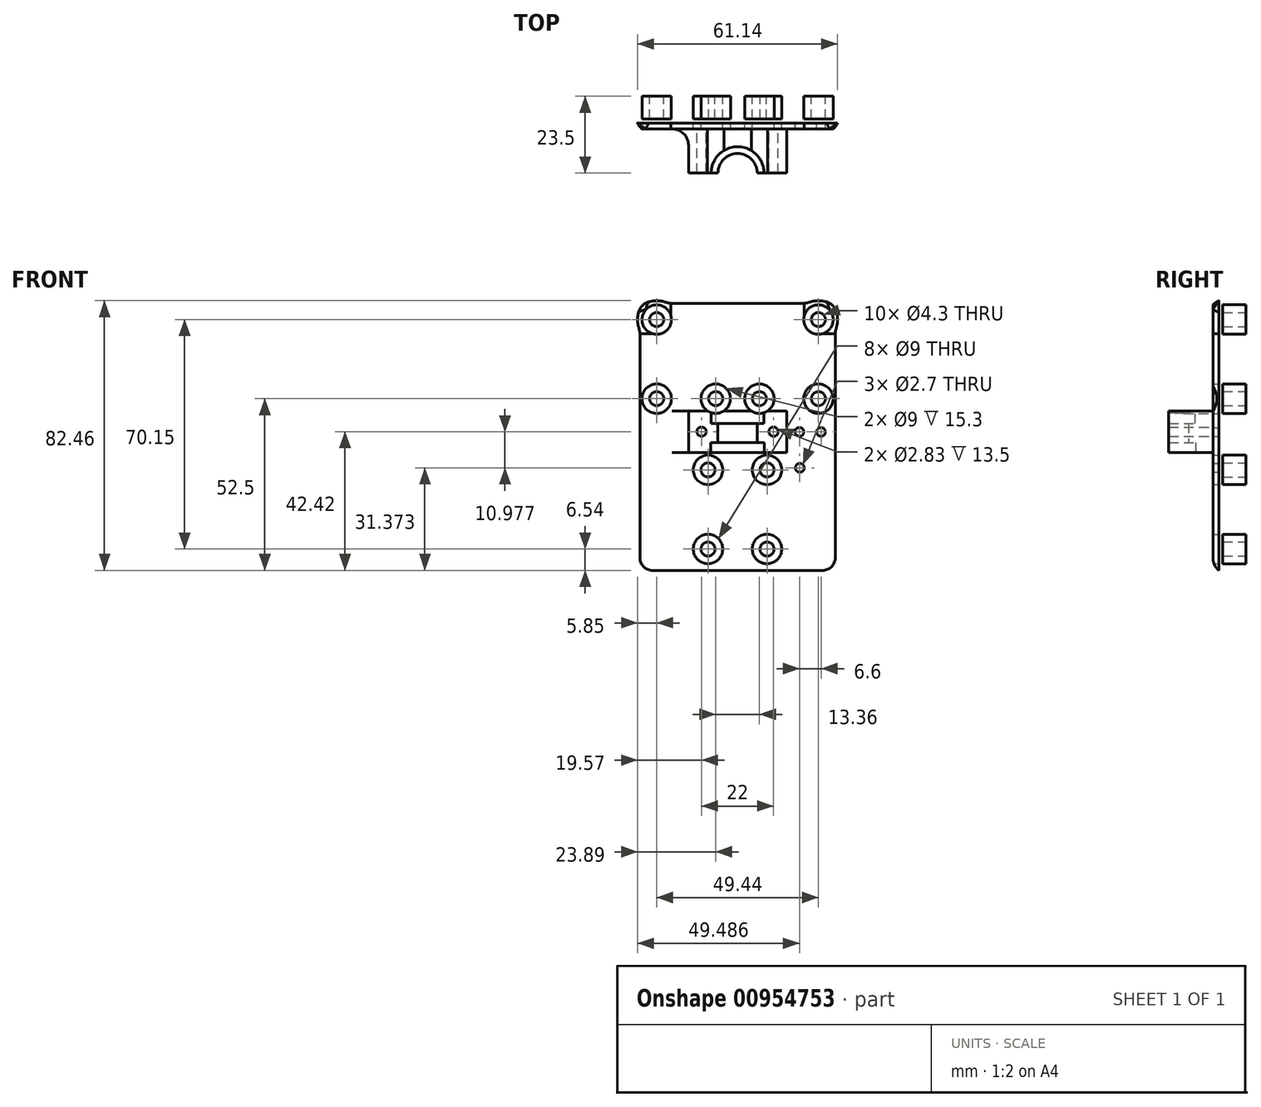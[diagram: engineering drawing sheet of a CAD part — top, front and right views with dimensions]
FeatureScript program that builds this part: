
annotation { "Feature Type Name" : "Feature", "Feature Type Description" : "" }
export const myFeature = defineFeature(function(context is Context, id is Id, definition is map)
    precondition{}
    {
        {
            var Q0;
            Q0=qCreatedBy(makeId("Front.planeOp"),FACE);
            var sketch = newSketch(context, id + "F0", { "sketchPlane" : qUnion([Q0])});
            skLineSegment(sketch, "E0.bottom", {"start": v(26, 42) * mm, "end": v(-26, 42) * mm});
            skLineSegment(sketch, "E0.top", {"start": v(26, -42) * mm, "end": v(-26, -42) * mm});
            skLineSegment(sketch, "E0.left", {"start": v(31, 37) * mm, "end": v(31, -37) * mm});
            skLineSegment(sketch, "E0.right", {"start": v(-31, 37) * mm, "end": v(-31, -37) * mm});
            skPoint(sketch, "E0.middle", {"position": v(1.18, -1.15) * mm});
            skPoint(sketch, "E1.visualSharp", {"position": v(-31, 42) * mm});
            skArc(sketch, "E1.filletArc", {"start": v(-26, 42) * mm, "mid": v(-29.54, 40.54) * mm, "end": v(-31, 37) * mm});
            skPoint(sketch, "E2.visualSharp", {"position": v(31, 42) * mm});
            skArc(sketch, "E2.filletArc", {"start": v(31, 37) * mm, "mid": v(29.54, 40.54) * mm, "end": v(26, 42) * mm});
            skPoint(sketch, "E3.visualSharp", {"position": v(31, -42) * mm});
            skArc(sketch, "E3.filletArc", {"start": v(26, -42) * mm, "mid": v(29.54, -40.54) * mm, "end": v(31, -37) * mm});
            skPoint(sketch, "E4.visualSharp", {"position": v(-31, -42) * mm});
            skArc(sketch, "E4.filletArc", {"start": v(-31, -37) * mm, "mid": v(-29.54, -40.54) * mm, "end": v(-26, -42) * mm});
            skCircle(sketch, "E5", {"center": v(-24.72, 35.85) * mm, "radius": 2.15 * mm});
            skCircle(sketch, "E6.0", {"center": v(-24.72, 35.85) * mm, "radius": 4.5 * mm});
            skCircle(sketch, "E7.1.0.0", {"center": v(-24.72, 11.66) * mm, "radius": 4.5 * mm});
            skCircle(sketch, "E7.1.0.1", {"center": v(-24.72, 11.66) * mm, "radius": 2.15 * mm});
            skCircle(sketch, "E7.1.0.2", {"center": v(-6.68, 11.66) * mm, "radius": 2.15 * mm});
            skCircle(sketch, "E7.1.0.3", {"center": v(-6.68, 11.66) * mm, "radius": 4.5 * mm});
            skCircle(sketch, "E8.1.0.2", {"center": v(6.68, 11.66) * mm, "radius": 4.5 * mm});
            skCircle(sketch, "E8.1.0.4", {"center": v(24.72, 11.66) * mm, "radius": 2.15 * mm});
            skCircle(sketch, "E8.1.0.5", {"center": v(6.68, 11.66) * mm, "radius": 2.15 * mm});
            skCircle(sketch, "E8.1.0.6", {"center": v(24.72, 35.85) * mm, "radius": 2.15 * mm});
            skCircle(sketch, "E8.1.0.7", {"center": v(24.72, 35.85) * mm, "radius": 4.5 * mm});
            skCircle(sketch, "E8.1.0.9", {"center": v(24.72, 11.66) * mm, "radius": 4.5 * mm});
            skCircle(sketch, "E9.1.0.0", {"center": v(-9.04, -10.1) * mm, "radius": 4.5 * mm});
            skCircle(sketch, "E9.1.0.1", {"center": v(-9.04, -10.1) * mm, "radius": 2.15 * mm});
            skCircle(sketch, "E9.1.0.2", {"center": v(9, -10.1) * mm, "radius": 2.15 * mm});
            skCircle(sketch, "E9.1.0.4", {"center": v(9, -10.1) * mm, "radius": 4.5 * mm});
            skCircle(sketch, "E9.1.0.6", {"center": v(-9.04, -34.3) * mm, "radius": 4.5 * mm});
            skCircle(sketch, "E9.1.0.7", {"center": v(9, -34.3) * mm, "radius": 4.5 * mm});
            skCircle(sketch, "E9.1.0.8", {"center": v(9, -34.3) * mm, "radius": 2.15 * mm});
            skCircle(sketch, "E9.1.0.9", {"center": v(-9.04, -34.3) * mm, "radius": 2.15 * mm});
            skCircle(sketch, "E10", {"center": v(-18.96, 1.51) * mm, "radius": 1.35 * mm});
            skCircle(sketch, "E11", {"center": v(-25.56, 1.51) * mm, "radius": 1.35 * mm});
            skCircle(sketch, "E12", {"center": v(-19.06, -9.47) * mm, "radius": 1.35 * mm});
            skCircle(sketch, "E13.MirrorC", {"center": v(18.92, 1.51) * mm, "radius": 1.35 * mm});
            skCircle(sketch, "E14.MirrorC", {"center": v(25.52, 1.51) * mm, "radius": 1.35 * mm});
            skCircle(sketch, "E15.MirrorC", {"center": v(19.01, -9.47) * mm, "radius": 1.35 * mm});
            skSolve(sketch);
        }
        {
            var Q0;
            Q0=makeQuery(id+"F0.imprint","IMPRINT",FACE,{"disambiguationData":[TD([[makeQuery(id+"F0.imprint","IMPRINT",EDGE,{"derivedFrom":sQuery(id+"F0.wireOp",EDGE,"E0.bottom")}),1.0]])]});
            var Q1;
            Q1=makeQuery(id+"F0.imprint","IMPRINT",FACE,{"disambiguationData":[TD([[makeQuery(id+"F0.imprint","IMPRINT",EDGE,{"derivedFrom":sQuery(id+"F0.wireOp",EDGE,"E11")}),1.0]])]});
            var Q2;
            Q2=makeQuery(id+"F0.imprint","IMPRINT",FACE,{"disambiguationData":[TD([[makeQuery(id+"F0.imprint","IMPRINT",EDGE,{"derivedFrom":sQuery(id+"F0.wireOp",EDGE,"E10")}),1.0]])]});
            var Q3;
            Q3=makeQuery(id+"F0.imprint","IMPRINT",FACE,{"disambiguationData":[TD([[makeQuery(id+"F0.imprint","IMPRINT",EDGE,{"derivedFrom":sQuery(id+"F0.wireOp",EDGE,"E12")}),1.0]])]});
            var Q4;
            Q4=makeQuery(id+"F0.imprint","IMPRINT",FACE,{"disambiguationData":[TD([[makeQuery(id+"F0.imprint","IMPRINT",EDGE,{"derivedFrom":sQuery(id+"F0.wireOp",EDGE,"E13.MirrorC")}),-1.0]])]});
            var Q5;
            Q5=makeQuery(id+"F0.imprint","IMPRINT",FACE,{"disambiguationData":[TD([[makeQuery(id+"F0.imprint","IMPRINT",EDGE,{"derivedFrom":sQuery(id+"F0.wireOp",EDGE,"E14.MirrorC")}),-1.0]])]});
            var Q6;
            Q6=makeQuery(id+"F0.imprint","IMPRINT",FACE,{"disambiguationData":[TD([[makeQuery(id+"F0.imprint","IMPRINT",EDGE,{"derivedFrom":sQuery(id+"F0.wireOp",EDGE,"E15.MirrorC")}),-1.0]])]});
            extrude(context, id + "F1", {"entities" : qUnion([Q0, Q1, Q2, Q3, Q4, Q5, Q6]), "depth" : 10 * mm});
        }
        {
            var Q0;
            Q0=makeQuery(id+"F0.imprint","IMPRINT",FACE,{"disambiguationData":[TD([[makeQuery(id+"F0.imprint","IMPRINT",EDGE,{"derivedFrom":sQuery(id+"F0.wireOp",EDGE,"E5")}),-1.0]])]});
            var Q1;
            Q1=makeQuery(id+"F0.imprint","IMPRINT",FACE,{"disambiguationData":[TD([[makeQuery(id+"F0.imprint","IMPRINT",EDGE,{"derivedFrom":sQuery(id+"F0.wireOp",EDGE,"92a26904-eb14-4965-84a8-ee2cf7e59395.1.0.0")}),-1.0]])]});
            var Q2;
            Q2=makeQuery(id+"F0.imprint","IMPRINT",FACE,{"disambiguationData":[TD([[makeQuery(id+"F0.imprint","IMPRINT",EDGE,{"derivedFrom":sQuery(id+"F0.wireOp",EDGE,"E8.1.0.0")}),1.0]])]});
            var Q3;
            Q3=makeQuery(id+"F0.imprint","IMPRINT",FACE,{"disambiguationData":[TD([[makeQuery(id+"F0.imprint","IMPRINT",EDGE,{"derivedFrom":sQuery(id+"F0.wireOp",EDGE,"E7.1.0.0")}),1.0]])]});
            var Q4;
            Q4=makeQuery(id+"F0.imprint","IMPRINT",FACE,{"disambiguationData":[TD([[makeQuery(id+"F0.imprint","IMPRINT",EDGE,{"derivedFrom":sQuery(id+"F0.wireOp",EDGE,"E7.1.0.2")}),-1.0]])]});
            var Q5;
            Q5=makeQuery(id+"F0.imprint","IMPRINT",FACE,{"disambiguationData":[TD([[makeQuery(id+"F0.imprint","IMPRINT",EDGE,{"derivedFrom":sQuery(id+"F0.wireOp",EDGE,"E8.1.0.2")}),1.0]])]});
            var Q6;
            Q6=makeQuery(id+"F0.imprint","IMPRINT",FACE,{"disambiguationData":[TD([[makeQuery(id+"F0.imprint","IMPRINT",EDGE,{"derivedFrom":sQuery(id+"F0.wireOp",EDGE,"E8.1.0.6")}),-1.0]])]});
            var Q7;
            Q7=makeQuery(id+"F0.imprint","IMPRINT",FACE,{"disambiguationData":[TD([[makeQuery(id+"F0.imprint","IMPRINT",EDGE,{"derivedFrom":sQuery(id+"F0.wireOp",EDGE,"E8.1.0.4")}),-1.0]])]});
            var Q8;
            Q8=makeQuery(id+"F0.imprint","IMPRINT",FACE,{"disambiguationData":[TD([[makeQuery(id+"F0.imprint","IMPRINT",EDGE,{"derivedFrom":sQuery(id+"F0.wireOp",EDGE,"E9.1.0.6")}),1.0]])]});
            var Q9;
            Q9=makeQuery(id+"F0.imprint","IMPRINT",FACE,{"disambiguationData":[TD([[makeQuery(id+"F0.imprint","IMPRINT",EDGE,{"derivedFrom":sQuery(id+"F0.wireOp",EDGE,"E9.1.0.7")}),1.0]])]});
            var Q10;
            Q10=makeQuery(id+"F0.imprint","IMPRINT",FACE,{"disambiguationData":[TD([[makeQuery(id+"F0.imprint","IMPRINT",EDGE,{"derivedFrom":sQuery(id+"F0.wireOp",EDGE,"E9.1.0.0")}),1.0]])]});
            var Q11;
            Q11=makeQuery(id+"F0.imprint","IMPRINT",FACE,{"disambiguationData":[TD([[makeQuery(id+"F0.imprint","IMPRINT",EDGE,{"derivedFrom":sQuery(id+"F0.wireOp",EDGE,"E9.1.0.2")}),-1.0]])]});
            extrude(context, id + "F2", {"entities" : qUnion([Q0, Q1, Q2, Q3, Q4, Q5, Q6, Q7, Q8, Q9, Q10, Q11]), "operationType" : NewBodyOperationType.ADD, "depth" : 7 * mm});
        }
        {
            var Q0;
            Q0=makeQuery(id+"F1.opExtrude","CAP_FACE",FACE,{"disambiguationData":[OSD([sQuery(id+"F0.wireOp",EDGE,"E0.bottom"),sQuery(id+"F0.wireOp",EDGE,"E0.top"),sQuery(id+"F0.wireOp",EDGE,"E0.left"),sQuery(id+"F0.wireOp",EDGE,"E0.right"),sQuery(id+"F0.wireOp",EDGE,"E1.filletArc"),sQuery(id+"F0.wireOp",EDGE,"E2.filletArc"),sQuery(id+"F0.wireOp",EDGE,"E3.filletArc"),sQuery(id+"F0.wireOp",EDGE,"E4.filletArc"),sQuery(id+"F0.wireOp",EDGE,"E6.0"),sQuery(id+"F0.wireOp",EDGE,"92a26904-eb14-4965-84a8-ee2cf7e59395.1.0.1"),sQuery(id+"F0.wireOp",EDGE,"E7.1.0.0"),sQuery(id+"F0.wireOp",EDGE,"E7.1.0.3"),sQuery(id+"F0.wireOp",EDGE,"E8.1.0.0"),sQuery(id+"F0.wireOp",EDGE,"E8.1.0.2"),sQuery(id+"F0.wireOp",EDGE,"E8.1.0.7"),sQuery(id+"F0.wireOp",EDGE,"E8.1.0.9"),sQuery(id+"F0.wireOp",EDGE,"E9.1.0.0"),sQuery(id+"F0.wireOp",EDGE,"E9.1.0.4"),sQuery(id+"F0.wireOp",EDGE,"E9.1.0.6"),sQuery(id+"F0.wireOp",EDGE,"E9.1.0.7")])],"isStart":false});
            var sketch = newSketch(context, id + "F3", { "sketchPlane" : qUnion([Q0])});
            skLineSegment(sketch, "E16", {"start": v(-26, -42) * mm, "end": v(0, -42) * mm});
            skLineSegment(sketch, "E17", {"start": v(0, -42) * mm, "end": v(26, -42) * mm});
            skLineSegment(sketch, "E18.bottom", {"start": v(15, 7.92) * mm, "end": v(-15, 7.92) * mm});
            skLineSegment(sketch, "E18.top", {"start": v(15, -4.76) * mm, "end": v(-15, -4.76) * mm});
            skLineSegment(sketch, "E18.left", {"start": v(15, 7.92) * mm, "end": v(15, -4.76) * mm});
            skLineSegment(sketch, "E18.right", {"start": v(-15, 7.92) * mm, "end": v(-15, -4.76) * mm});
            skPoint(sketch, "E18.middle", {"position": v(0, 1.58) * mm});
            skPoint(sketch, "E19.endSnap0", {"position": v(0, 7.92) * mm});
            skLineSegment(sketch, "E20.bottom", {"start": v(-5, -3.14) * mm, "end": v(-5, -3.14) * mm});
            skLineSegment(sketch, "E20.top", {"start": v(0, -12.45) * mm, "end": v(0, -12.45) * mm});
            skLineSegment(sketch, "E21", {"start": v(-15, 1.58) * mm, "end": v(-11, 1.58) * mm});
            skLineSegment(sketch, "E22", {"start": v(15, 1.58) * mm, "end": v(11, 1.58) * mm});
            skCircle(sketch, "E23", {"center": v(-11, 1.58) * mm, "radius": 1.42 * mm});
            skCircle(sketch, "E24.MirrorC", {"center": v(11, 1.58) * mm, "radius": 1.42 * mm});
            skSolve(sketch);
        }
        {
            var Q0;
            Q0=makeQuery(id+"F1.opExtrude","CAP_EDGE",EDGE,{"disambiguationData":[OSD([sQuery(id+"F0.wireOp",EDGE,"E0.left")])],"isStart":false});
            var Q1;
            Q1=makeQuery(id+"F1.opExtrude","CAP_EDGE",EDGE,{"disambiguationData":[OSD([sQuery(id+"F0.wireOp",EDGE,"E0.bottom")])],"isStart":false});
            var Q2;
            Q2=makeQuery(id+"F1.opExtrude","CAP_EDGE",EDGE,{"disambiguationData":[OSD([sQuery(id+"F0.wireOp",EDGE,"E2.filletArc")])],"isStart":false});
            var Q3;
            Q3=makeQuery(id+"F1.opExtrude","CAP_EDGE",EDGE,{"disambiguationData":[OSD([sQuery(id+"F0.wireOp",EDGE,"E1.filletArc")])],"isStart":false});
            var Q4;
            Q4=makeQuery(id+"F1.opExtrude","CAP_EDGE",EDGE,{"disambiguationData":[OSD([sQuery(id+"F0.wireOp",EDGE,"E0.right")])],"isStart":false});
            var Q5;
            Q5=makeQuery(id+"F1.opExtrude","CAP_EDGE",EDGE,{"disambiguationData":[OSD([sQuery(id+"F0.wireOp",EDGE,"E4.filletArc")])],"isStart":false});
            var Q6;
            Q6=makeQuery(id+"F1.opExtrude","CAP_EDGE",EDGE,{"disambiguationData":[OSD([sQuery(id+"F0.wireOp",EDGE,"E0.top")])],"isStart":false});
            var Q7;
            Q7=makeQuery(id+"F1.opExtrude","CAP_EDGE",EDGE,{"disambiguationData":[OSD([sQuery(id+"F0.wireOp",EDGE,"E3.filletArc")])],"isStart":false});
            fillet(context, id + "F4", {"entities" : qUnion([Q0, Q1, Q2, Q3, Q4, Q5, Q6, Q7]), "radius" : 5 * mm, "tangentPropagation" : true, "allowEdgeOverflow" : false});
        }
        {
            var Q0;
            Q0=makeQuery(id+"F3.imprint","IMPRINT",FACE,{"disambiguationData":[TD([[makeQuery(id+"F3.imprint","IMPRINT",EDGE,{"derivedFrom":sQuery(id+"F3.wireOp",EDGE,"E18.bottom")}),1.0]])]});
            extrude(context, id + "F5", {"entities" : qUnion([Q0]), "operationType" : NewBodyOperationType.ADD, "depth" : 13.5 * mm});
        }
        {
            var Q0;
            Q0=makeQuery(id+"F5.opExtrude","SWEPT_FACE",FACE,{"disambiguationData":[OSD([sQuery(id+"F3.wireOp",EDGE,"E18.top")])]});
            var sketch = newSketch(context, id + "F6", { "sketchPlane" : qUnion([Q0])});
            skSolve(sketch);
        }
        {
            var Q0;
            {var subQ0=sQuery(id+"F3.wireOp",EDGE,"E18.top");Q0=makeQuery(id+"F6.imprint","IMPRINT",FACE,{"disambiguationData":[TD([[makeQuery(id+"F6.imprint","IMPRINT",EDGE,{"derivedFrom":makeQuery(id+"F5.opExtrude","CAP_EDGE",EDGE,{"disambiguationData":[OSD([subQ0])],"isStart":false})}),1.0]])]});}
            var sketch = newSketch(context, id + "F7", { "sketchPlane" : qUnion([Q0])});
            skLineSegment(sketch, "E25", {"start": v(0, 23.5) * mm, "end": v(-6, 23.5) * mm});
            skLineSegment(sketch, "E26.MirrorCS", {"start": v(0, 23.5) * mm, "end": v(6, 23.5) * mm});
            skArc(sketch, "E27", {"start": v(-6, 23.5) * mm, "mid": v(0, 17.52) * mm, "end": v(6, 23.5) * mm});
            skArc(sketch, "E28.0", {"start": v(-8.17, 23.5) * mm, "mid": v(0, 15.35) * mm, "end": v(8.17, 23.5) * mm});
            skLineSegment(sketch, "E29", {"start": v(-8.17, 23.5) * mm, "end": v(-6, 23.5) * mm});
            skLineSegment(sketch, "E30", {"start": v(6, 23.5) * mm, "end": v(8.17, 23.5) * mm});
            skSolve(sketch);
        }
        {
            var Q0;
            Q0=makeQuery(id+"F5.opExtrude","SWEPT_FACE",FACE,{"disambiguationData":[OSD([sQuery(id+"F3.wireOp",EDGE,"E18.bottom")])]});
            var sketch = newSketch(context, id + "F8", { "sketchPlane" : qUnion([Q0])});
            skLineSegment(sketch, "E31", {"start": v(0.1, -23.5) * mm, "end": v(-5.9, -23.5) * mm});
            skLineSegment(sketch, "E32", {"start": v(-5.9, -23.5) * mm, "end": v(-5.9, -23.5) * mm});
            skArc(sketch, "E33.0", {"start": v(8.07, -23.5) * mm, "mid": v(0, -15.43) * mm, "end": v(-8.07, -23.5) * mm});
            skLineSegment(sketch, "E34", {"start": v(8.07, -23.5) * mm, "end": v(-5.9, -23.5) * mm});
            skLineSegment(sketch, "E35", {"start": v(-5.9, -23.5) * mm, "end": v(-8.07, -23.5) * mm});
            skSolve(sketch);
        }
        {
            var Q0;
            {var subQ1=sQuery(id+"F7.wireOp",EDGE,"E28.0");Q0=makeQuery(id+"F7.imprint","IMPRINT",FACE,{"disambiguationData":[TD([[makeQuery(id+"F7.imprint","IMPRINT",EDGE,{"derivedFrom":subQ1}),1.0]])]});}
            extrude(context, id + "F9", {"entities" : qUnion([Q0]), "operationType" : NewBodyOperationType.REMOVE, "oppositeDirection" : true, "depth" : 3 * mm});
        }
        {
            var Q0;
            Q0=makeQuery(id+"F8.imprint","IMPRINT",FACE,{"disambiguationData":[TD([[makeQuery(id+"F8.imprint","IMPRINT",EDGE,{"derivedFrom":sQuery(id+"F8.wireOp",EDGE,"E32")}),-1.0]])]});
            var Q1;
            {var subQ0=sQuery(id+"F8.wireOp",EDGE,"E34");var subQ1=sQuery(id+"F8.wireOp",EDGE,"E33.0");var subQ2=makeQuery(id+"F8.imprint","INTERSECT",VERTEX,{"derivedFrom":[subQ1,subQ0]});Q1=makeQuery(id+"F8.imprint","IMPRINT",FACE,{"disambiguationData":[TD([[makeQuery(id+"F8.imprint","IMPRINT",EDGE,{"disambiguationData":[TD([[subQ2,-1.0]])],"derivedFrom":subQ1}),1.0]])]});}
            var Q2;
            {var subQ0=sQuery(id+"F8.wireOp",EDGE,"E33.0");var subQ1=sQuery(id+"F3.wireOp",EDGE,"E18.bottom");var subQ2=sQuery(id+"F0.wireOp",EDGE,"E8.1.0.2");var subQ3=makeQuery(id+"F5.opExtrude","SWEPT_EDGE",EDGE,{"disambiguationData":[OSD([subQ2,subQ1]),TDD([makeQuery(id+"F3.imprint","INTERSECT",VERTEX,{"disambiguationData":[OD(1.0)],"derivedFrom":[makeQuery(id+"F1.opExtrude","CAP_EDGE",EDGE,{"disambiguationData":[OSD([subQ2])],"isStart":false}),subQ1]})])]});var subQ4=makeQuery(id+"F8.imprint","INTERSECT",VERTEX,{"derivedFrom":[subQ3,subQ0]});Q2=makeQuery(id+"F8.imprint","IMPRINT",FACE,{"disambiguationData":[TD([[makeQuery(id+"F8.imprint","IMPRINT",EDGE,{"disambiguationData":[TD([[subQ4,-1.0]])],"derivedFrom":subQ0}),1.0]])]});}
            var Q3;
            {var subQ0=sQuery(id+"F8.wireOp",EDGE,"E35");Q3=makeQuery(id+"F8.imprint","IMPRINT",FACE,{"disambiguationData":[TD([[makeQuery(id+"F8.imprint","IMPRINT",EDGE,{"derivedFrom":subQ0}),-1.0]])]});}
            extrude(context, id + "F10", {"entities" : qUnion([Q0, Q1, Q2, Q3]), "operationType" : NewBodyOperationType.REMOVE, "oppositeDirection" : true, "depth" : 3.8 * mm, "offsetDistance" : 25 * mm});
        }
        {
            var Q0;
            Q0=makeQuery(id+"F5.opExtrude","CAP_EDGE",EDGE,{"disambiguationData":[OSD([sQuery(id+"F3.wireOp",EDGE,"E18.right")])],"isStart":true});
            fillet(context, id + "F11", {"entities" : qUnion([Q0]), "radius" : 5 * mm, "tangentPropagation" : true, "allowEdgeOverflow" : false});
        }
        {
            var Q0;
            {var subQ0=sQuery(id+"F7.wireOp",EDGE,"E27");var subQ1=makeQuery(id+"F6.imprint","IMPRINT",EDGE,{"derivedFrom":makeQuery(id+"F5.opExtrude","CAP_EDGE",EDGE,{"disambiguationData":[OSD([sQuery(id+"F3.wireOp",EDGE,"E18.top")])],"isStart":false})});var subQ2=makeQuery(id+"F7.imprint","INTERSECT",VERTEX,{"disambiguationData":[OD(0.0)],"derivedFrom":[subQ1,subQ0]});Q0=makeQuery(id+"F7.imprint","IMPRINT",FACE,{"disambiguationData":[TD([[makeQuery(id+"F7.imprint","IMPRINT",EDGE,{"disambiguationData":[TD([[subQ2,-1.0]])],"derivedFrom":subQ0}),1.0]])]});}
            extrude(context, id + "F12", {"entities" : qUnion([Q0]), "operationType" : NewBodyOperationType.REMOVE, "oppositeDirection" : true, "depth" : 25 * mm});
        }
        {
            var Q0;
            Q0=makeQuery(id+"F0.imprint","IMPRINT",FACE,{"disambiguationData":[TD([[makeQuery(id+"F0.imprint","IMPRINT",EDGE,{"derivedFrom":sQuery(id+"F0.wireOp",EDGE,"E14.MirrorC")}),-1.0]])]});
            var Q1;
            Q1=makeQuery(id+"F0.imprint","IMPRINT",FACE,{"disambiguationData":[TD([[makeQuery(id+"F0.imprint","IMPRINT",EDGE,{"derivedFrom":sQuery(id+"F0.wireOp",EDGE,"E13.MirrorC")}),-1.0]])]});
            var Q2;
            Q2=makeQuery(id+"F0.imprint","IMPRINT",FACE,{"disambiguationData":[TD([[makeQuery(id+"F0.imprint","IMPRINT",EDGE,{"derivedFrom":sQuery(id+"F0.wireOp",EDGE,"E15.MirrorC")}),-1.0]])]});
            var Q3;
            Q3=makeQuery(id+"F0.imprint","IMPRINT",FACE,{"disambiguationData":[TD([[makeQuery(id+"F0.imprint","IMPRINT",EDGE,{"derivedFrom":sQuery(id+"F0.wireOp",EDGE,"E12")}),1.0]])]});
            var Q4;
            Q4=makeQuery(id+"F0.imprint","IMPRINT",FACE,{"disambiguationData":[TD([[makeQuery(id+"F0.imprint","IMPRINT",EDGE,{"derivedFrom":sQuery(id+"F0.wireOp",EDGE,"E11")}),1.0]])]});
            var Q5;
            Q5=makeQuery(id+"F0.imprint","IMPRINT",FACE,{"disambiguationData":[TD([[makeQuery(id+"F0.imprint","IMPRINT",EDGE,{"derivedFrom":sQuery(id+"F0.wireOp",EDGE,"E10")}),1.0]])]});
            extrude(context, id + "F13", {"entities" : qUnion([Q0, Q1, Q2, Q3, Q4, Q5]), "operationType" : NewBodyOperationType.REMOVE, "depth" : 8.2 * mm});
        }
    });
